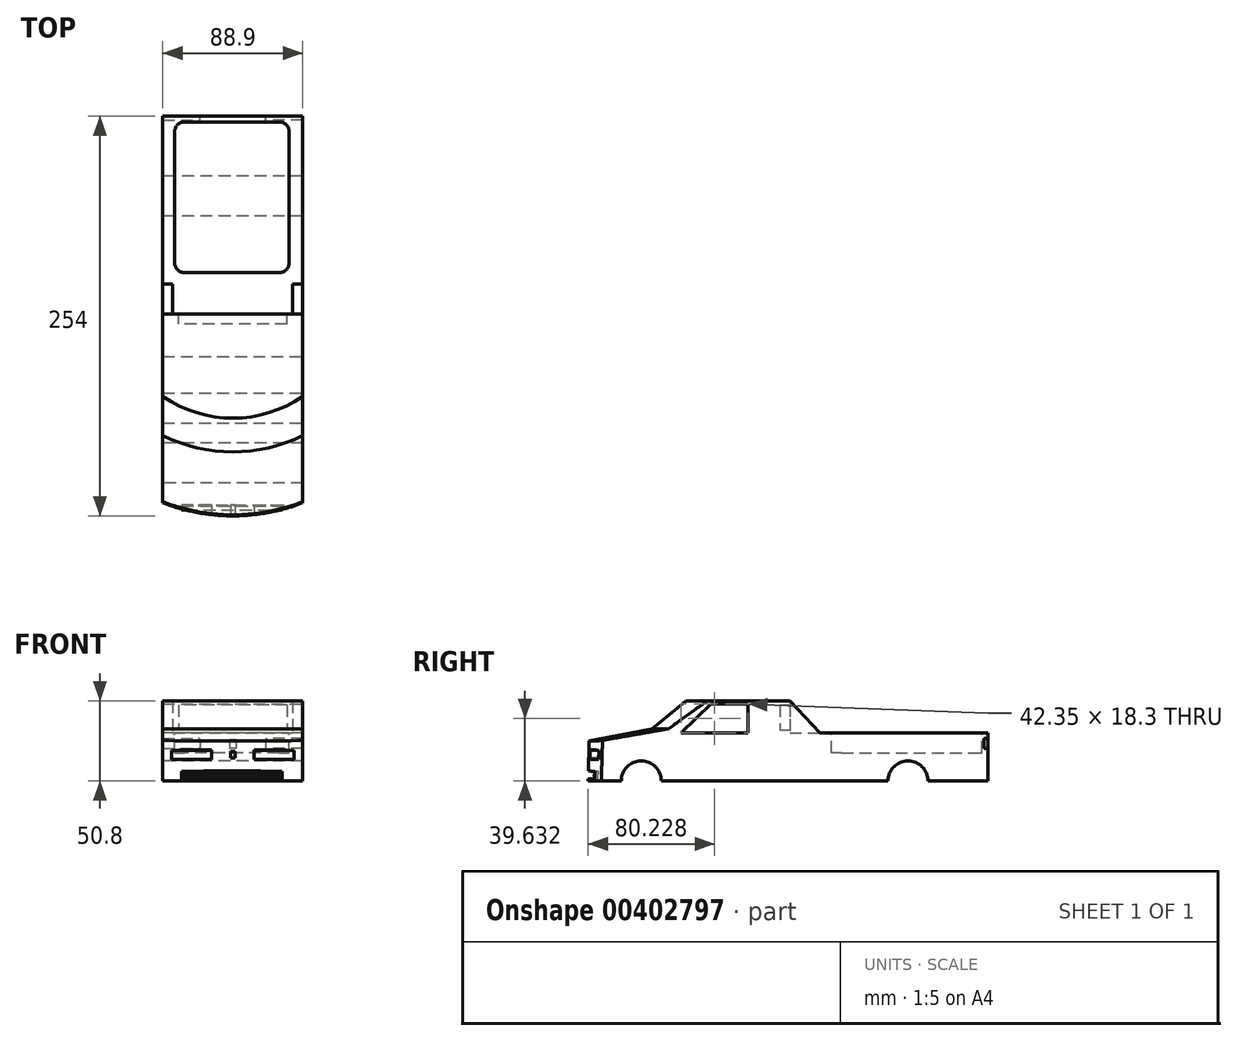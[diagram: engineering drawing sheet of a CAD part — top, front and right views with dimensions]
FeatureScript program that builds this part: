
annotation { "Feature Type Name" : "Feature", "Feature Type Description" : "" }
export const myFeature = defineFeature(function(context is Context, id is Id, definition is map)
    precondition{}
    {
        {
            var Q0;
            Q0=qCreatedBy(makeId("Right.planeOp"),FACE);
            var sketch = newSketch(context, id + "F0", { "sketchPlane" : qUnion([Q0])});
            skLineSegment(sketch, "E0", {"start": v(-147.32, -30.48) * mm, "end": v(-147.32, -30.48) * mm});
            skLineSegment(sketch, "E1", {"start": v(-147.32, -30.48) * mm, "end": v(-146.62, -5.09) * mm});
            skLineSegment(sketch, "E2", {"start": v(106.68, -30.48) * mm, "end": v(106.68, 0) * mm});
            skLineSegment(sketch, "E3", {"start": v(106.68, 0) * mm, "end": v(0, 0) * mm});
            skLineSegment(sketch, "E4", {"start": v(0, 0) * mm, "end": v(-19.18, 20.32) * mm});
            skLineSegment(sketch, "E5", {"start": v(-19.18, 20.32) * mm, "end": v(-85.22, 20.32) * mm});
            skLineSegment(sketch, "E6", {"start": v(-85.22, 20.32) * mm, "end": v(-106.68, 2.43) * mm});
            skLineSegment(sketch, "E7", {"start": v(-146.62, -5.09) * mm, "end": v(-106.68, 2.43) * mm});
            skLineSegment(sketch, "E8.trimOffspring", {"start": v(-147.32, -30.48) * mm, "end": v(106.68, -30.48) * mm});
            skLineSegment(sketch, "E9.trimOffspring", {"start": v(106.68, -30.48) * mm, "end": v(106.68, -30.48) * mm});
            skSolve(sketch);
        }
        {
            var Q0;
            Q0=makeQuery(id+"F0.imprint","IMPRINT",FACE,{"disambiguationData":[TD([[makeQuery(id+"F0.imprint","IMPRINT",EDGE,{"derivedFrom":sQuery(id+"F0.wireOp",EDGE,"E1")}),-1.0]])]});
            extrude(context, id + "F1", {"entities" : qUnion([Q0]), "endBound" : BoundingType.SYMMETRIC, "depth" : 88.9 * mm});
        }
        {
            var Q0;
            Q0=qCreatedBy(makeId("Right.planeOp"),FACE);
            var sketch = newSketch(context, id + "F2", { "sketchPlane" : qUnion([Q0])});
            skLineSegment(sketch, "E10.0", {"start": v(-62.36, 39.37) * mm, "end": v(-106.68, 2.43) * mm});
            skLineSegment(sketch, "E11.0", {"start": v(-179.07, -11.2) * mm, "end": v(-106.68, 2.43) * mm});
            skLineSegment(sketch, "E12", {"start": v(-179.07, -11.2) * mm, "end": v(-179.07, 39.37) * mm});
            skLineSegment(sketch, "E13", {"start": v(-179.07, 39.37) * mm, "end": v(-62.36, 39.37) * mm});
            skPoint(sketch, "E14.orphan", {"position": v(-85.22, 20.32) * mm});
            skLineSegment(sketch, "E15", {"start": v(-6.35, 20.15) * mm, "end": v(-6.35, 82.8) * mm, "construction": true});
            skPoint(sketch, "E16.orphan", {"position": v(-146.62, -5.09) * mm});
            skSolve(sketch);
        }
        {
            var Q0;
            Q0 = qSketchRegion(id + "F2", true);
            var Q1;
            Q1=sQuery(id+"F2.wireOp",EDGE,"E15");
            revolve(context, id + "F3", {"operationType" : NewBodyOperationType.REMOVE, "entities" : qUnion([Q0]), "axis" : qUnion([Q1]), "revolveType" : RevolveType.SYMMETRIC, "oppositeDirection" : true, "angle" : 180 * degree});
        }
        {
            var Q0;
            Q0=makeQuery(id+"F1.opExtrude","SWEPT_FACE",FACE,{"disambiguationData":[OSD([sQuery(id+"F0.wireOp",EDGE,"E3")])]});
            var sketch = newSketch(context, id + "F4", { "sketchPlane" : qUnion([Q0])});
            skLineSegment(sketch, "E17.bottom", {"start": v(29.46, 7.2) * mm, "end": v(-30.64, 7.2) * mm});
            skLineSegment(sketch, "E17.top", {"start": v(29.46, 102.97) * mm, "end": v(-30.64, 102.97) * mm});
            skLineSegment(sketch, "E17.left", {"start": v(35.81, 13.55) * mm, "end": v(35.81, 96.62) * mm});
            skLineSegment(sketch, "E17.right", {"start": v(-37, 13.55) * mm, "end": v(-37, 96.62) * mm});
            skPoint(sketch, "E18.visualSharp", {"position": v(35.81, 7.2) * mm});
            skArc(sketch, "E18.filletArc", {"start": v(29.46, 7.2) * mm, "mid": v(33.95, 9.06) * mm, "end": v(35.81, 13.55) * mm});
            skPoint(sketch, "E19.visualSharp", {"position": v(-37, 7.2) * mm});
            skArc(sketch, "E19.filletArc", {"start": v(-37, 13.55) * mm, "mid": v(-35.13, 9.06) * mm, "end": v(-30.64, 7.2) * mm});
            skPoint(sketch, "E20.visualSharp", {"position": v(-37, 102.97) * mm});
            skArc(sketch, "E20.filletArc", {"start": v(-30.64, 102.97) * mm, "mid": v(-35.13, 101.11) * mm, "end": v(-37, 96.62) * mm});
            skPoint(sketch, "E21.visualSharp", {"position": v(35.81, 102.97) * mm});
            skArc(sketch, "E21.filletArc", {"start": v(35.81, 96.62) * mm, "mid": v(33.95, 101.11) * mm, "end": v(29.46, 102.97) * mm});
            skSolve(sketch);
        }
        {
            var Q0;
            Q0 = qSketchRegion(id + "F4", true);
            extrude(context, id + "F5", {"entities" : qUnion([Q0]), "operationType" : NewBodyOperationType.REMOVE, "oppositeDirection" : true, "depth" : 12.7 * mm});
        }
        {
            var Q0;
            Q0=qCreatedBy(makeId("Right.planeOp"),FACE);
            var sketch = newSketch(context, id + "F6", { "sketchPlane" : qUnion([Q0])});
            skLineSegment(sketch, "E22.0", {"start": v(-147.32, -30.48) * mm, "end": v(-146.14, 12.1) * mm});
            skLineSegment(sketch, "E23", {"start": v(-25.1, 20.33) * mm, "end": v(-25.1, 58.65) * mm, "construction": true});
            skLineSegment(sketch, "E24", {"start": v(-147.32, -30.48) * mm, "end": v(-181.23, -30.48) * mm});
            skLineSegment(sketch, "E25", {"start": v(-181.23, -30.48) * mm, "end": v(-181.23, 12.1) * mm});
            skLineSegment(sketch, "E26", {"start": v(-181.23, 12.1) * mm, "end": v(-146.14, 12.1) * mm});
            skPoint(sketch, "E27.orphan", {"position": v(-146.65, -6.4) * mm});
            skSolve(sketch);
        }
        {
            var Q0;
            Q0=qCreatedBy(makeId("Right.planeOp"),FACE);
            var sketch = newSketch(context, id + "F7", { "sketchPlane" : qUnion([Q0])});
            skLineSegment(sketch, "E28.bottom", {"start": v(-19.18, 20.32) * mm, "end": v(0, 20.32) * mm});
            skLineSegment(sketch, "E28.top", {"start": v(-19.18, 0) * mm, "end": v(0, 0) * mm});
            skLineSegment(sketch, "E28.left", {"start": v(-19.18, 20.32) * mm, "end": v(-19.18, 0) * mm});
            skLineSegment(sketch, "E28.right", {"start": v(0, 20.32) * mm, "end": v(0, 0) * mm});
            skSolve(sketch);
        }
        {
            var Q0;
            Q0 = qSketchRegion(id + "F7", true);
            extrude(context, id + "F8", {"entities" : qUnion([Q0]), "operationType" : NewBodyOperationType.REMOVE, "endBound" : BoundingType.SYMMETRIC, "oppositeDirection" : true, "depth" : 76.2 * mm});
        }
        {
            var Q0;
            Q0=makeQuery(id+"F8.boolean.opBoolean","COPY",FACE,{"derivedFrom":makeQuery(id+"F8.opExtrude","SWEPT_FACE",FACE,{"disambiguationData":[OSD([sQuery(id+"F7.wireOp",EDGE,"E28.left")])]})});
            var sketch = newSketch(context, id + "F9", { "sketchPlane" : qUnion([Q0])});
            skLineSegment(sketch, "E29.bottom", {"start": v(-34.4, 17.63) * mm, "end": v(34.42, 17.63) * mm});
            skLineSegment(sketch, "E29.top", {"start": v(-34.4, 1.95) * mm, "end": v(34.42, 1.95) * mm});
            skLineSegment(sketch, "E29.left", {"start": v(-34.4, 17.63) * mm, "end": v(-34.4, 1.95) * mm});
            skLineSegment(sketch, "E29.right", {"start": v(34.42, 17.63) * mm, "end": v(34.42, 1.95) * mm});
            skSolve(sketch);
        }
        {
            var Q0;
            Q0 = qSketchRegion(id + "F9", true);
            extrude(context, id + "F10", {"entities" : qUnion([Q0]), "operationType" : NewBodyOperationType.REMOVE, "oppositeDirection" : true, "depth" : 6.35 * mm});
        }
        {
            var Q0;
            Q0=makeQuery(id+"F1.opExtrude","SWEPT_FACE",FACE,{"disambiguationData":[OSD([sQuery(id+"F0.wireOp",EDGE,"E2")])]});
            var sketch = newSketch(context, id + "F11", { "sketchPlane" : qUnion([Q0])});
            skLineSegment(sketch, "E30", {"start": v(0, 0) * mm, "end": v(0, -30.48) * mm, "construction": true});
            skLineSegment(sketch, "E31.bottom", {"start": v(-44.45, -3.65) * mm, "end": v(-21.59, -3.65) * mm});
            skLineSegment(sketch, "E31.top", {"start": v(-44.45, -10) * mm, "end": v(-21.59, -10) * mm});
            skLineSegment(sketch, "E31.left", {"start": v(-44.45, -3.65) * mm, "end": v(-44.45, -10) * mm});
            skLineSegment(sketch, "E32", {"start": v(-20.83, -4.41) * mm, "end": v(-20.83, -9.24) * mm});
            skPoint(sketch, "E33.visualSharp", {"position": v(-20.83, -3.65) * mm});
            skArc(sketch, "E33.filletArc", {"start": v(-20.83, -4.41) * mm, "mid": v(-21.05, -3.87) * mm, "end": v(-21.59, -3.65) * mm});
            skPoint(sketch, "E34.visualSharp", {"position": v(-20.83, -10) * mm});
            skArc(sketch, "E34.filletArc", {"start": v(-21.59, -10) * mm, "mid": v(-21.05, -9.77) * mm, "end": v(-20.83, -9.24) * mm});
            skLineSegment(sketch, "E35.MirrorCS", {"start": v(44.45, -3.65) * mm, "end": v(21.59, -3.65) * mm});
            skLineSegment(sketch, "E36.MirrorCS", {"start": v(20.83, -4.41) * mm, "end": v(20.83, -9.24) * mm});
            skArc(sketch, "E37.MirrorCS", {"start": v(20.83, -4.41) * mm, "mid": v(21.05, -3.87) * mm, "end": v(21.59, -3.65) * mm});
            skArc(sketch, "E38.MirrorCS", {"start": v(21.59, -10) * mm, "mid": v(21.05, -9.77) * mm, "end": v(20.83, -9.24) * mm});
            skLineSegment(sketch, "E39.MirrorCS", {"start": v(44.45, -10) * mm, "end": v(21.59, -10) * mm});
            skLineSegment(sketch, "E40.MirrorCS", {"start": v(44.45, -3.65) * mm, "end": v(44.45, -10) * mm});
            skSolve(sketch);
        }
        {
            var Q0;
            Q0 = qSketchRegion(id + "F11", true);
            extrude(context, id + "F12", {"entities" : qUnion([Q0]), "operationType" : NewBodyOperationType.REMOVE, "oppositeDirection" : true, "depth" : 2.54 * mm});
        }
        {
            var Q0;
            Q0=qCreatedBy(makeId("Right.planeOp"),FACE);
            var sketch = newSketch(context, id + "F13", { "sketchPlane" : qUnion([Q0])});
            skLineSegment(sketch, "E41.bottom", {"start": v(-45.92, 0) * mm, "end": v(-88.27, 0) * mm});
            skLineSegment(sketch, "E41.top", {"start": v(-45.92, 18.3) * mm, "end": v(-69.16, 18.3) * mm});
            skLineSegment(sketch, "E41.left", {"start": v(-45.92, 0) * mm, "end": v(-45.92, 18.3) * mm});
            skLineSegment(sketch, "E41.right", {"start": v(-88.27, 0) * mm, "end": v(-69.16, 18.3) * mm});
            skSolve(sketch);
        }
        {
            var Q0;
            Q0 = qSketchRegion(id + "F13", true);
            extrude(context, id + "F14", {"entities" : qUnion([Q0]), "operationType" : NewBodyOperationType.REMOVE, "endBound" : BoundingType.THROUGH_ALL, "oppositeDirection" : true, "depth" : 25.4 * mm, "hasSecondDirection" : true, "secondDirectionBound" : SecondDirectionBoundingType.THROUGH_ALL, "secondDirectionOppositeDirection" : false, "secondDirectionDepth" : 25.4 * mm});
        }
        {
            var Q0;
            Q0=makeQuery(id+"F1.opExtrude","SWEPT_FACE",FACE,{"disambiguationData":[OSD([sQuery(id+"F0.wireOp",EDGE,"E2")])]});
            var sketch = newSketch(context, id + "F15", { "sketchPlane" : qUnion([Q0])});
            skLineSegment(sketch, "E42.bottom", {"start": v(-2.17, -4.38) * mm, "end": v(2.18, -4.38) * mm});
            skLineSegment(sketch, "E42.top", {"start": v(-2.17, -9.9) * mm, "end": v(2.18, -9.9) * mm});
            skLineSegment(sketch, "E42.left", {"start": v(-2.17, -4.38) * mm, "end": v(-2.17, -9.9) * mm});
            skLineSegment(sketch, "E42.right", {"start": v(2.18, -4.38) * mm, "end": v(2.18, -9.9) * mm});
            skSolve(sketch);
        }
        {
            var Q0;
            Q0 = qSketchRegion(id + "F15", true);
            extrude(context, id + "F16", {"entities" : qUnion([Q0]), "operationType" : NewBodyOperationType.REMOVE, "oppositeDirection" : true, "depth" : 0.25 * mm});
        }
        {
            var Q0;
            Q0=makeQuery(id+"F1.opExtrude","SWEPT_FACE",FACE,{"disambiguationData":[OSD([sQuery(id+"F0.wireOp",EDGE,"E1")])]});
            var sketch = newSketch(context, id + "F17", { "sketchPlane" : qUnion([Q0])});
            skLineSegment(sketch, "E43.bottom", {"start": v(-13.59, -20.85) * mm, "end": v(-44.45, -20.85) * mm});
            skLineSegment(sketch, "E43.top", {"start": v(-13.59, -14.88) * mm, "end": v(-44.45, -14.88) * mm});
            skLineSegment(sketch, "E43.left", {"start": v(-13.59, -20.85) * mm, "end": v(-13.59, -14.88) * mm});
            skLineSegment(sketch, "E43.right", {"start": v(-44.45, -20.85) * mm, "end": v(-44.45, -14.88) * mm});
            skLineSegment(sketch, "E44.0", {"start": v(0, -35.48) * mm, "end": v(0, 7.09) * mm, "construction": true});
            skLineSegment(sketch, "E45.MirrorCS", {"start": v(13.59, -20.85) * mm, "end": v(13.59, -14.88) * mm});
            skLineSegment(sketch, "E46.MirrorCS", {"start": v(13.59, -14.88) * mm, "end": v(44.45, -14.88) * mm});
            skLineSegment(sketch, "E47.MirrorCS", {"start": v(13.59, -20.85) * mm, "end": v(44.45, -20.85) * mm});
            skLineSegment(sketch, "E48.MirrorCS", {"start": v(44.45, -20.85) * mm, "end": v(44.45, -14.88) * mm});
            skLineSegment(sketch, "E49.bottom", {"start": v(1.44, -19.79) * mm, "end": v(-1.44, -19.79) * mm});
            skLineSegment(sketch, "E49.top", {"start": v(1.44, -15.84) * mm, "end": v(-1.44, -15.84) * mm});
            skLineSegment(sketch, "E49.left", {"start": v(1.44, -19.79) * mm, "end": v(1.44, -15.84) * mm});
            skLineSegment(sketch, "E49.right", {"start": v(-1.44, -19.79) * mm, "end": v(-1.44, -15.84) * mm});
            skPoint(sketch, "E50", {"position": v(0, -15.84) * mm});
            skPoint(sketch, "E51", {"position": v(0, -19.79) * mm});
            skLineSegment(sketch, "E52.bottom", {"start": v(31.42, -33.34) * mm, "end": v(-32.43, -33.34) * mm});
            skLineSegment(sketch, "E52.top", {"start": v(31.42, -28.32) * mm, "end": v(-32.43, -28.32) * mm});
            skLineSegment(sketch, "E52.left", {"start": v(31.42, -33.34) * mm, "end": v(31.42, -28.32) * mm});
            skLineSegment(sketch, "E52.right", {"start": v(-32.43, -33.34) * mm, "end": v(-32.43, -28.32) * mm});
            skLineSegment(sketch, "E53.left", {"start": v(-32.43, -30.83) * mm, "end": v(-32.43, -31.7) * mm});
            skLineSegment(sketch, "E53.right", {"start": v(31.42, -30.83) * mm, "end": v(31.42, -31.7) * mm});
            skSolve(sketch);
        }
        {
            var Q0;
            Q0 = qSketchRegion(id + "F17", true);
            extrude(context, id + "F18", {"entities" : qUnion([Q0]), "operationType" : NewBodyOperationType.REMOVE, "oppositeDirection" : true, "depth" : 6.35 * mm});
        }
        {
            var Q0;
            Q0 = qSketchRegion(id + "F6", true);
            var Q1;
            Q1=sQuery(id+"F6.wireOp",EDGE,"E23");
            revolve(context, id + "F19", {"operationType" : NewBodyOperationType.REMOVE, "entities" : qUnion([Q0]), "axis" : qUnion([Q1]), "revolveType" : RevolveType.SYMMETRIC, "oppositeDirection" : true, "angle" : 140 * degree});
        }
        {
            var Q0;
            Q0=qCreatedBy(makeId("Right.planeOp"),FACE);
            var sketch = newSketch(context, id + "F20", { "sketchPlane" : qUnion([Q0])});
            skLineSegment(sketch, "E54.0", {"start": v(-138.95, -30.48) * mm, "end": v(-126.25, -30.48) * mm, "construction": true});
            skFitSpline(sketch, "E54.1", {"points": [v(-138.95, -30.48) * mm, v(-138.7, -21.95) * mm, v(-138.44, -13.41) * mm, v(-138.19, -4.88) * mm], "construction": true});
            skFitSpline(sketch, "E54.2", {"points": [v(-138.19, -4.88) * mm, v(-131.21, -3.63) * mm, v(-117.25, -1.16) * mm, v(-103.28, 1.25) * mm, v(-96.3, 2.43) * mm], "construction": true});
            skFitSpline(sketch, "E54.3", {"points": [v(-71.5, 20.32) * mm, v(-75.7, 17.43) * mm, v(-84.01, 11.53) * mm, v(-92.21, 5.48) * mm, v(-96.3, 2.43) * mm], "construction": true});
            skLineSegment(sketch, "E54.4", {"start": v(-19.18, 20.32) * mm, "end": v(-71.5, 20.32) * mm, "construction": true});
            skLineSegment(sketch, "E54.5", {"start": v(0, 0) * mm, "end": v(-19.18, 20.32) * mm, "construction": true});
            skLineSegment(sketch, "E54.6", {"start": v(106.68, 0) * mm, "end": v(0, 0) * mm, "construction": true});
            skLineSegment(sketch, "E54.7", {"start": v(106.68, -30.48) * mm, "end": v(106.68, 0) * mm, "construction": true});
            skArc(sketch, "E55", {"start": v(-100.85, -30.48) * mm, "mid": v(-113.55, -17.78) * mm, "end": v(-126.25, -30.48) * mm});
            skArc(sketch, "E56", {"start": v(68.58, -30.48) * mm, "mid": v(55.88, -17.78) * mm, "end": v(43.18, -30.48) * mm});
            skLineSegment(sketch, "E57", {"start": v(55.88, -30.48) * mm, "end": v(55.88, 0) * mm, "construction": true});
            skLineSegment(sketch, "E58", {"start": v(-113.55, -30.48) * mm, "end": v(-113.55, -0.53) * mm, "construction": true});
            skLineSegment(sketch, "E59.trimOffspring", {"start": v(68.58, -30.48) * mm, "end": v(106.68, -30.48) * mm, "construction": true});
            skLineSegment(sketch, "E60.trimOffspring", {"start": v(-100.85, -30.48) * mm, "end": v(43.18, -30.48) * mm, "construction": true});
            skLineSegment(sketch, "E61", {"start": v(-126.25, -30.48) * mm, "end": v(-100.85, -30.48) * mm});
            skLineSegment(sketch, "E62", {"start": v(43.18, -30.48) * mm, "end": v(68.58, -30.48) * mm});
            skSolve(sketch);
        }
        {
            var Q0;
            Q0 = qSketchRegion(id + "F20", true);
            extrude(context, id + "F21", {"entities" : qUnion([Q0]), "operationType" : NewBodyOperationType.REMOVE, "endBound" : BoundingType.THROUGH_ALL, "depth" : 25.4 * mm, "hasSecondDirection" : true, "secondDirectionBound" : SecondDirectionBoundingType.THROUGH_ALL, "secondDirectionOppositeDirection" : true, "secondDirectionDepth" : 25.4 * mm});
        }
        {
            var Q0;
            Q0=makeQuery(id+"F18.boolean.opBoolean","COPY",FACE,{"derivedFrom":makeQuery(id+"F18.opExtrude","CAP_FACE",FACE,{"disambiguationData":[OSD([sQuery(id+"F17.wireOp",EDGE,"E52.bottom"),sQuery(id+"F17.wireOp",EDGE,"E52.top"),sQuery(id+"F17.wireOp",EDGE,"E52.left"),sQuery(id+"F17.wireOp",EDGE,"E52.right"),sQuery(id+"F17.wireOp",EDGE,"E53.left"),sQuery(id+"F17.wireOp",EDGE,"E53.right")])],"isStart":false})});
            var sketch = newSketch(context, id + "F22", { "sketchPlane" : qUnion([Q0])});
            skLineSegment(sketch, "E63.bottom", {"start": v(-32.43, -30.2) * mm, "end": v(31.42, -30.2) * mm});
            skLineSegment(sketch, "E63.top", {"start": v(-32.43, -31.46) * mm, "end": v(31.42, -31.46) * mm});
            skLineSegment(sketch, "E63.left", {"start": v(-32.43, -30.2) * mm, "end": v(-32.43, -31.46) * mm});
            skLineSegment(sketch, "E63.right", {"start": v(31.42, -30.2) * mm, "end": v(31.42, -31.46) * mm});
            skSolve(sketch);
        }
        {
            var Q0;
            Q0 = qSketchRegion(id + "F22", true);
            extrude(context, id + "F23", {"entities" : qUnion([Q0]), "operationType" : NewBodyOperationType.ADD, "depth" : 2.54 * mm});
        }
    });
